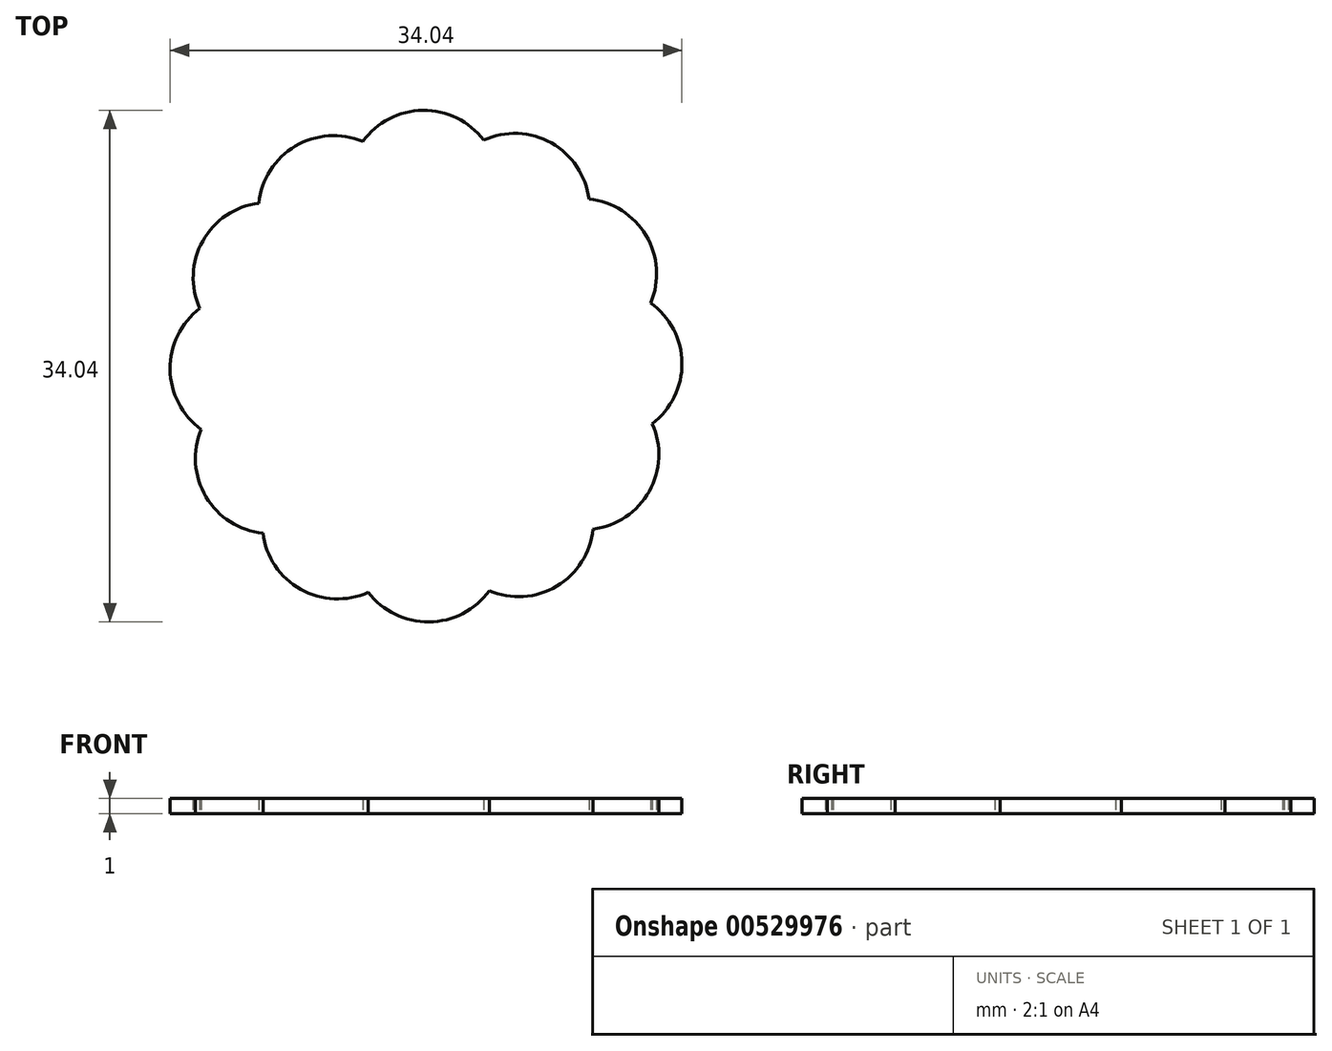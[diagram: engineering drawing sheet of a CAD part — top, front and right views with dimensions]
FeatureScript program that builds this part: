
annotation { "Feature Type Name" : "Feature", "Feature Type Description" : "" }
export const myFeature = defineFeature(function(context is Context, id is Id, definition is map)
    precondition{}
    {
        {
            var Q0;
            Q0=qCreatedBy(makeId("Top.planeOp"),FACE);
            var sketch = newSketch(context, id + "F0", { "sketchPlane" : qUnion([Q0])});
            skCircle(sketch, "E0.cCircle", {"center": v(0, 0) * mm, "radius": 15 * mm, "construction": true});
            skLineSegment(sketch, "E0.0", {"start": v(15.05, -3.83) * mm, "end": v(11.11, -10.85) * mm});
            skLineSegment(sketch, "E0.1", {"start": v(11.11, -10.85) * mm, "end": v(4.2, -14.95) * mm});
            skLineSegment(sketch, "E0.2", {"start": v(4.2, -14.95) * mm, "end": v(-3.83, -15.05) * mm});
            skLineSegment(sketch, "E0.3", {"start": v(-3.83, -15.05) * mm, "end": v(-10.85, -11.11) * mm});
            skLineSegment(sketch, "E0.4", {"start": v(-10.85, -11.11) * mm, "end": v(-14.95, -4.2) * mm});
            skLineSegment(sketch, "E0.5", {"start": v(-14.95, -4.2) * mm, "end": v(-15.05, 3.83) * mm});
            skLineSegment(sketch, "E0.6", {"start": v(-15.05, 3.83) * mm, "end": v(-11.11, 10.85) * mm});
            skLineSegment(sketch, "E0.7", {"start": v(-11.11, 10.85) * mm, "end": v(-4.2, 14.95) * mm});
            skLineSegment(sketch, "E0.8", {"start": v(-4.2, 14.95) * mm, "end": v(3.83, 15.05) * mm});
            skLineSegment(sketch, "E0.9", {"start": v(3.83, 15.05) * mm, "end": v(10.85, 11.11) * mm});
            skLineSegment(sketch, "E0.10", {"start": v(10.85, 11.11) * mm, "end": v(14.95, 4.2) * mm});
            skLineSegment(sketch, "E0.11", {"start": v(14.95, 4.2) * mm, "end": v(15.05, -3.83) * mm});
            skPoint(sketch, "E0.0.midPoint", {"position": v(13.08, -7.34) * mm});
            skArc(sketch, "E1", {"start": v(-11.11, 10.85) * mm, "mid": v(-14.85, 8.33) * mm, "end": v(-15.05, 3.83) * mm});
            skArc(sketch, "E2", {"start": v(-4.2, 14.95) * mm, "mid": v(-8.7, 14.64) * mm, "end": v(-11.11, 10.85) * mm});
            skArc(sketch, "E3", {"start": v(3.83, 15.05) * mm, "mid": v(-0.2, 17.02) * mm, "end": v(-4.2, 14.95) * mm});
            skArc(sketch, "E4", {"start": v(10.85, 11.11) * mm, "mid": v(8.33, 14.85) * mm, "end": v(3.83, 15.05) * mm});
            skArc(sketch, "E5", {"start": v(14.95, 4.2) * mm, "mid": v(14.64, 8.7) * mm, "end": v(10.85, 11.11) * mm});
            skArc(sketch, "E6", {"start": v(15.05, -3.83) * mm, "mid": v(17.02, 0.2) * mm, "end": v(14.95, 4.2) * mm});
            skArc(sketch, "E7", {"start": v(11.11, -10.85) * mm, "mid": v(14.85, -8.33) * mm, "end": v(15.05, -3.83) * mm});
            skArc(sketch, "E8", {"start": v(4.2, -14.95) * mm, "mid": v(8.7, -14.64) * mm, "end": v(11.11, -10.85) * mm});
            skArc(sketch, "E9", {"start": v(-3.83, -15.05) * mm, "mid": v(0.2, -17.02) * mm, "end": v(4.2, -14.95) * mm});
            skArc(sketch, "E10", {"start": v(-10.85, -11.11) * mm, "mid": v(-8.33, -14.85) * mm, "end": v(-3.83, -15.05) * mm});
            skArc(sketch, "E11", {"start": v(-14.95, -4.2) * mm, "mid": v(-14.64, -8.7) * mm, "end": v(-10.85, -11.11) * mm});
            skArc(sketch, "E12", {"start": v(-15.05, 3.83) * mm, "mid": v(-17.02, -0.2) * mm, "end": v(-14.95, -4.2) * mm});
            skCircle(sketch, "E13.cCircle", {"center": v(0, 0) * mm, "radius": 4.3 * mm, "construction": true});
            skLineSegment(sketch, "E13.0", {"start": v(4.3, 0) * mm, "end": v(2.15, -3.72) * mm});
            skLineSegment(sketch, "E13.1", {"start": v(2.15, -3.72) * mm, "end": v(-2.15, -3.72) * mm});
            skLineSegment(sketch, "E13.2", {"start": v(-2.15, -3.72) * mm, "end": v(-4.3, 0) * mm});
            skLineSegment(sketch, "E13.3", {"start": v(-4.3, 0) * mm, "end": v(-2.15, 3.72) * mm});
            skLineSegment(sketch, "E13.4", {"start": v(-2.15, 3.72) * mm, "end": v(2.15, 3.72) * mm});
            skLineSegment(sketch, "E13.5", {"start": v(2.15, 3.72) * mm, "end": v(4.3, 0) * mm});
            skSolve(sketch);
        }
        {
            var Q0;
            Q0=makeQuery(id+"F0.imprint","IMPRINT",FACE,{"disambiguationData":[TD([[makeQuery(id+"F0.imprint","IMPRINT",EDGE,{"derivedFrom":sQuery(id+"F0.wireOp",EDGE,"E0.0")}),-1.0]])]});
            var Q1;
            Q1=makeQuery(id+"F0.imprint","IMPRINT",FACE,{"disambiguationData":[TD([[makeQuery(id+"F0.imprint","IMPRINT",EDGE,{"derivedFrom":sQuery(id+"F0.wireOp",EDGE,"E0.2")}),1.0]])]});
            var Q2;
            Q2=makeQuery(id+"F0.imprint","IMPRINT",FACE,{"disambiguationData":[TD([[makeQuery(id+"F0.imprint","IMPRINT",EDGE,{"derivedFrom":sQuery(id+"F0.wireOp",EDGE,"E0.5")}),1.0]])]});
            var Q3;
            Q3=makeQuery(id+"F0.imprint","IMPRINT",FACE,{"disambiguationData":[TD([[makeQuery(id+"F0.imprint","IMPRINT",EDGE,{"derivedFrom":sQuery(id+"F0.wireOp",EDGE,"E0.10")}),1.0]])]});
            var Q4;
            Q4=makeQuery(id+"F0.imprint","IMPRINT",FACE,{"disambiguationData":[TD([[makeQuery(id+"F0.imprint","IMPRINT",EDGE,{"derivedFrom":sQuery(id+"F0.wireOp",EDGE,"E0.0")}),1.0]])]});
            var Q5;
            Q5=makeQuery(id+"F0.imprint","IMPRINT",FACE,{"disambiguationData":[TD([[makeQuery(id+"F0.imprint","IMPRINT",EDGE,{"derivedFrom":sQuery(id+"F0.wireOp",EDGE,"E0.1")}),1.0]])]});
            var Q6;
            Q6=makeQuery(id+"F0.imprint","IMPRINT",FACE,{"disambiguationData":[TD([[makeQuery(id+"F0.imprint","IMPRINT",EDGE,{"derivedFrom":sQuery(id+"F0.wireOp",EDGE,"E0.3")}),1.0]])]});
            var Q7;
            Q7=makeQuery(id+"F0.imprint","IMPRINT",FACE,{"disambiguationData":[TD([[makeQuery(id+"F0.imprint","IMPRINT",EDGE,{"derivedFrom":sQuery(id+"F0.wireOp",EDGE,"E0.4")}),1.0]])]});
            var Q8;
            Q8=makeQuery(id+"F0.imprint","IMPRINT",FACE,{"disambiguationData":[TD([[makeQuery(id+"F0.imprint","IMPRINT",EDGE,{"derivedFrom":sQuery(id+"F0.wireOp",EDGE,"E0.6")}),1.0]])]});
            var Q9;
            Q9=makeQuery(id+"F0.imprint","IMPRINT",FACE,{"disambiguationData":[TD([[makeQuery(id+"F0.imprint","IMPRINT",EDGE,{"derivedFrom":sQuery(id+"F0.wireOp",EDGE,"E0.8")}),1.0]])]});
            var Q10;
            Q10=makeQuery(id+"F0.imprint","IMPRINT",FACE,{"disambiguationData":[TD([[makeQuery(id+"F0.imprint","IMPRINT",EDGE,{"derivedFrom":sQuery(id+"F0.wireOp",EDGE,"E0.9")}),1.0]])]});
            var Q11;
            Q11=makeQuery(id+"F0.imprint","IMPRINT",FACE,{"disambiguationData":[TD([[makeQuery(id+"F0.imprint","IMPRINT",EDGE,{"derivedFrom":sQuery(id+"F0.wireOp",EDGE,"E0.11")}),1.0]])]});
            var Q12;
            Q12=makeQuery(id+"F0.imprint","IMPRINT",FACE,{"disambiguationData":[TD([[makeQuery(id+"F0.imprint","IMPRINT",EDGE,{"derivedFrom":sQuery(id+"F0.wireOp",EDGE,"E13.0")}),-1.0]])]});
            var Q13;
            Q13=makeQuery(id+"F0.imprint","IMPRINT",FACE,{"disambiguationData":[TD([[makeQuery(id+"F0.imprint","IMPRINT",EDGE,{"derivedFrom":sQuery(id+"F0.wireOp",EDGE,"E0.7")}),1.0]])]});
            extrude(context, id + "F1", {"entities" : qUnion([Q0, Q1, Q2, Q3, Q4, Q5, Q6, Q7, Q8, Q9, Q10, Q11, Q12, Q13]), "depth" : 1 * mm, "offsetDistance" : 25 * mm});
        }
    });
